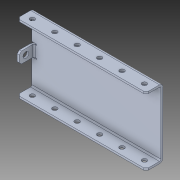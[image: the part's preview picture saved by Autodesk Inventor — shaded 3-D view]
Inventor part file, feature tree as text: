
AUTODESK INVENTOR PART (.ipt)
format: ipt  version: 2018 (Build 220112000, 112)  size: 126,464 bytes
history: native  units: in
note: dims shown in document units (in); Inventor stores cm internally (conversion verified against a paired STEP export)
features: chamfer x1
ambient origin geometry x8: Origin, YZ Plane, XZ Plane, XY Plane, X Axis, Y Axis, Z Axis, Center Point
bodies: Solid1 (feature_tree)
feature tree (1):
  chamfer  "Chamfer1"  [1 undecoded]
note: 1 required parameter value undecoded (feature->parameter linkage not recoverable at this tier; creation-order binding heuristic only, values carry confidence <= 0.55)
